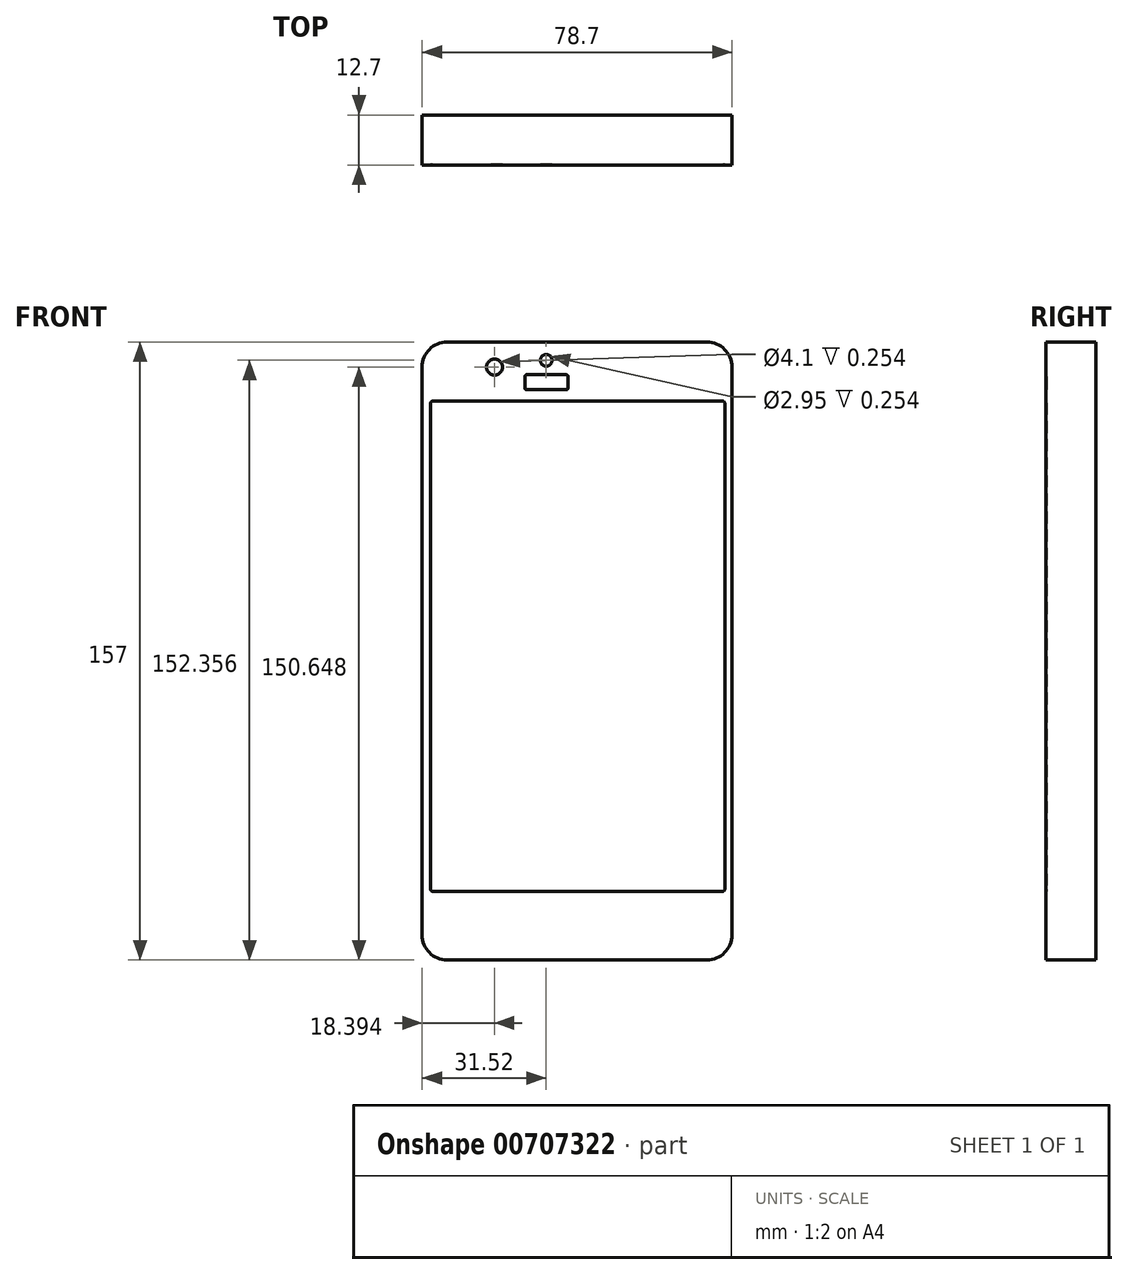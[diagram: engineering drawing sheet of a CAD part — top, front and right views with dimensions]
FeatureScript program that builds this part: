
annotation { "Feature Type Name" : "Feature", "Feature Type Description" : "" }
export const myFeature = defineFeature(function(context is Context, id is Id, definition is map)
    precondition{}
    {
        {
            var Q0;
            Q0=qCreatedBy(makeId("Front.planeOp"),FACE);
            var sketch = newSketch(context, id + "F0", { "sketchPlane" : qUnion([Q0])});
            skLineSegment(sketch, "E0.bottom", {"start": v(-25.17, 93.6) * mm, "end": v(40.83, 93.6) * mm});
            skLineSegment(sketch, "E0.top", {"start": v(-25.17, -63.4) * mm, "end": v(40.83, -63.4) * mm});
            skLineSegment(sketch, "E0.left", {"start": v(-31.52, 87.25) * mm, "end": v(-31.52, -57.05) * mm});
            skLineSegment(sketch, "E0.right", {"start": v(47.18, 87.25) * mm, "end": v(47.18, -57.05) * mm});
            skPoint(sketch, "E1.visualSharp", {"position": v(-31.52, 93.6) * mm});
            skArc(sketch, "E1.filletArc", {"start": v(-25.17, 93.6) * mm, "mid": v(-29.66, 91.74) * mm, "end": v(-31.52, 87.25) * mm});
            skPoint(sketch, "E2.visualSharp", {"position": v(47.18, 93.6) * mm});
            skArc(sketch, "E2.filletArc", {"start": v(47.18, 87.25) * mm, "mid": v(45.32, 91.74) * mm, "end": v(40.83, 93.6) * mm});
            skPoint(sketch, "E3.visualSharp", {"position": v(47.18, -63.4) * mm});
            skArc(sketch, "E3.filletArc", {"start": v(40.83, -63.4) * mm, "mid": v(45.32, -61.54) * mm, "end": v(47.18, -57.05) * mm});
            skPoint(sketch, "E4.visualSharp", {"position": v(-31.52, -63.4) * mm});
            skArc(sketch, "E4.filletArc", {"start": v(-31.52, -57.05) * mm, "mid": v(-29.66, -61.54) * mm, "end": v(-25.17, -63.4) * mm});
            skSolve(sketch);
        }
        {
            var Q0;
            Q0 = qSketchRegion(id + "F0", true);
            extrude(context, id + "F1", {"entities" : qUnion([Q0]), "depth" : 12.7 * mm, "offsetDistance" : 25.4 * mm});
        }
        {
            var Q0;
            Q0=makeQuery(id+"F1.opExtrude","CAP_FACE",FACE,{"disambiguationData":[OSD([sQuery(id+"F0.wireOp",EDGE,"E0.bottom"),sQuery(id+"F0.wireOp",EDGE,"E0.top"),sQuery(id+"F0.wireOp",EDGE,"E0.left"),sQuery(id+"F0.wireOp",EDGE,"E0.right"),sQuery(id+"F0.wireOp",EDGE,"E1.filletArc"),sQuery(id+"F0.wireOp",EDGE,"E2.filletArc"),sQuery(id+"F0.wireOp",EDGE,"E3.filletArc"),sQuery(id+"F0.wireOp",EDGE,"E4.filletArc")])],"isStart":false});
            var sketch = newSketch(context, id + "F2", { "sketchPlane" : qUnion([Q0])});
            skCircle(sketch, "E5", {"center": v(-13.13, 87.25) * mm, "radius": 2.05 * mm});
            skCircle(sketch, "E6", {"center": v(0, 88.96) * mm, "radius": 1.47 * mm});
            skLineSegment(sketch, "E7.bottom", {"start": v(-4.94, 85.3) * mm, "end": v(5.07, 85.3) * mm});
            skLineSegment(sketch, "E7.top", {"start": v(-4.94, 81.47) * mm, "end": v(5.07, 81.47) * mm});
            skLineSegment(sketch, "E7.left", {"start": v(-5.4, 84.85) * mm, "end": v(-5.4, 81.92) * mm});
            skLineSegment(sketch, "E7.right", {"start": v(5.52, 84.85) * mm, "end": v(5.52, 81.92) * mm});
            skPoint(sketch, "E8.visualSharp", {"position": v(-5.4, 85.3) * mm});
            skArc(sketch, "E8.filletArc", {"start": v(-4.94, 85.3) * mm, "mid": v(-5.26, 85.17) * mm, "end": v(-5.4, 84.85) * mm});
            skPoint(sketch, "E9.visualSharp", {"position": v(-5.4, 81.47) * mm});
            skArc(sketch, "E9.filletArc", {"start": v(-5.4, 81.92) * mm, "mid": v(-5.26, 81.6) * mm, "end": v(-4.94, 81.47) * mm});
            skPoint(sketch, "E10.visualSharp", {"position": v(5.52, 81.47) * mm});
            skArc(sketch, "E10.filletArc", {"start": v(5.07, 81.47) * mm, "mid": v(5.39, 81.6) * mm, "end": v(5.52, 81.92) * mm});
            skPoint(sketch, "E11.visualSharp", {"position": v(5.52, 85.3) * mm});
            skArc(sketch, "E11.filletArc", {"start": v(5.52, 84.85) * mm, "mid": v(5.39, 85.17) * mm, "end": v(5.07, 85.3) * mm});
            skLineSegment(sketch, "E12.bottom", {"start": v(-28.89, 78.56) * mm, "end": v(44.9, 78.56) * mm});
            skLineSegment(sketch, "E12.top", {"start": v(-28.89, -45.95) * mm, "end": v(44.9, -45.95) * mm});
            skLineSegment(sketch, "E12.left", {"start": v(-29.34, 78.11) * mm, "end": v(-29.34, -45.5) * mm});
            skLineSegment(sketch, "E12.right", {"start": v(45.35, 78.11) * mm, "end": v(45.35, -45.5) * mm});
            skPoint(sketch, "E13.visualSharp", {"position": v(-29.34, 78.56) * mm});
            skArc(sketch, "E13.filletArc", {"start": v(-28.89, 78.56) * mm, "mid": v(-29.2, 78.43) * mm, "end": v(-29.34, 78.11) * mm});
            skPoint(sketch, "E14.visualSharp", {"position": v(45.35, 78.56) * mm});
            skArc(sketch, "E14.filletArc", {"start": v(45.35, 78.11) * mm, "mid": v(45.22, 78.43) * mm, "end": v(44.9, 78.56) * mm});
            skPoint(sketch, "E15.visualSharp", {"position": v(45.35, -45.95) * mm});
            skArc(sketch, "E15.filletArc", {"start": v(44.9, -45.95) * mm, "mid": v(45.22, -45.81) * mm, "end": v(45.35, -45.5) * mm});
            skPoint(sketch, "E16.visualSharp", {"position": v(-29.34, -45.95) * mm});
            skArc(sketch, "E16.filletArc", {"start": v(-29.34, -45.5) * mm, "mid": v(-29.2, -45.81) * mm, "end": v(-28.89, -45.95) * mm});
            skCircle(sketch, "E17", {"center": v(6.4, -54.92) * mm, "radius": 6.8 * mm});
            skCircle(sketch, "E18", {"center": v(6.4, -54.92) * mm, "radius": 5.3 * mm});
            skSolve(sketch);
        }
        {
            var Q0;
            Q0=makeQuery(id+"F2.imprint","IMPRINT",FACE,{"disambiguationData":[TD([[makeQuery(id+"F2.imprint","IMPRINT",EDGE,{"derivedFrom":sQuery(id+"F2.wireOp",EDGE,"E5")}),1.0]])]});
            var Q1;
            Q1=makeQuery(id+"F2.imprint","IMPRINT",FACE,{"disambiguationData":[TD([[makeQuery(id+"F2.imprint","IMPRINT",EDGE,{"derivedFrom":sQuery(id+"F2.wireOp",EDGE,"E6")}),1.0]])]});
            var Q2;
            Q2=makeQuery(id+"F2.imprint","IMPRINT",FACE,{"disambiguationData":[TD([[makeQuery(id+"F2.imprint","IMPRINT",EDGE,{"derivedFrom":sQuery(id+"F2.wireOp",EDGE,"E7.bottom")}),-1.0]])]});
            var Q3;
            Q3=makeQuery(id+"F2.imprint","IMPRINT",FACE,{"disambiguationData":[TD([[makeQuery(id+"F2.imprint","IMPRINT",EDGE,{"derivedFrom":sQuery(id+"F2.wireOp",EDGE,"fv0aMx3Z-NzTv-aTEu-f3Rz-LBknOMsLS8Os")}),1.0]])]});
            var Q4;
            Q4=makeQuery(id+"F2.imprint","IMPRINT",FACE,{"disambiguationData":[TD([[makeQuery(id+"F2.imprint","IMPRINT",EDGE,{"derivedFrom":sQuery(id+"F2.wireOp",EDGE,"E12.bottom")}),-1.0]])]});
            extrude(context, id + "F3", {"entities" : qUnion([Q0, Q1, Q2, Q3, Q4]), "operationType" : NewBodyOperationType.REMOVE, "oppositeDirection" : true, "depth" : 0.25 * mm, "offsetDistance" : 25.4 * mm});
        }
        {
            var Q0;
            Q0=sQuery(id+"F2.wireOp",EDGE,"E17");
            extrude(context, id + "F4", {"bodyType" : ToolBodyType.SURFACE, "surfaceEntities" : qUnion([Q0]), "depth" : .1 * mm, "offsetDistance" : 25.4 * mm});
        }
    });
